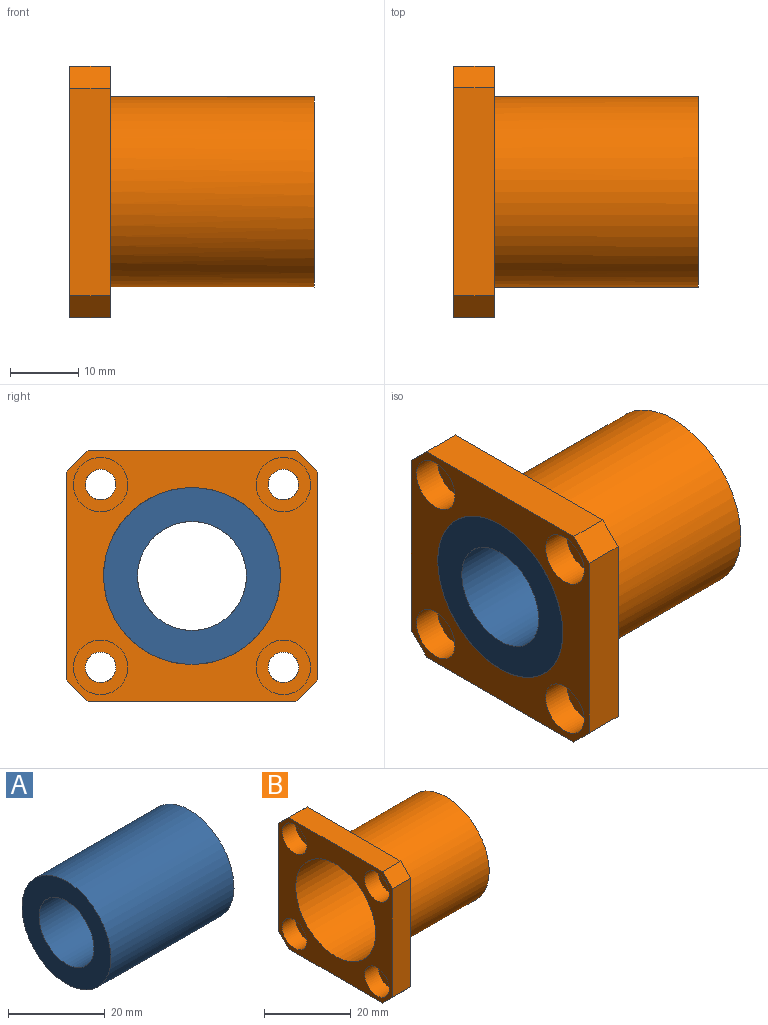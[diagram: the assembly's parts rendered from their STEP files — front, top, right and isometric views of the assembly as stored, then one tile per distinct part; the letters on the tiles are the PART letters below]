
ASSEMBLY  parts=2 mates=1
PART A: 4 faces, bbox 36x26x26 mm
  f0: plane 26x26mm, normal (1,0,0), area 329.9mm2, adj f2,f3
  f1: plane 26x26mm, normal (-1,0,0), area 329.9mm2, adj f2,f3
  f2: cylinder r=13mm len=36mm, axis (-1,0,0), area 2940.5mm2, adj f0,f1
  f3: cylinder r=8mm len=36mm, axis (-1,0,0), area 1809.6mm2, adj f0,f1
PART B: 25 faces, bbox 36x37x37 mm
  f0: cylinder r=2.25mm len=4.5mm, axis (-1,0,0), area 22.6mm2, adj f12,f19
  f1: cylinder r=2.25mm len=4.5mm, axis (-1,0,0), area 22.6mm2, adj f12,f17
  f2: cylinder r=2.25mm len=4.5mm, axis (-1,0,0), area 22.6mm2, adj f12,f15
  f3: cylinder r=2.25mm len=4.5mm, axis (-1,0,0), area 22.6mm2, adj f12,f21
  f4: plane 30.58x6mm, normal (0,0,-1), area 183.5mm2, adj f5,f11,f12,f13
  f5: plane 6x3.21mm, normal (0,0.71,-0.71), area 27.2mm2, adj f4,f6,f12,f13
  f6: plane 30.58x6mm, normal (0,1,0), area 183.5mm2, adj f5,f7,f12,f13
  f7: plane 6x3.21mm, normal (0,0.71,0.71), area 27.2mm2, adj f6,f8,f12,f13
  f8: plane 30.58x6mm, normal (0,0,1), area 183.5mm2, adj f7,f9,f12,f13
  f9: plane 6x3.21mm, normal (0,-0.71,0.71), area 27.2mm2, adj f8,f10,f12,f13
  f10: plane 30.58x6mm, normal (0,-1,0), area 183.5mm2, adj f9,f11,f12,f13
  f11: plane 6x3.21mm, normal (0,-0.71,-0.71), area 27.2mm2, adj f4,f10,f12,f13
  f12: plane 37x37mm, normal (1,0,0), area 669mm2, adj f0,f1,f2,f3,f4,f5,f6,f7
  f13: plane 37x37mm, normal (-1,0,0), area 616.4mm2, adj f4,f5,f6,f7,f8,f9,f10,f11
  f14: cylinder r=4mm len=8mm, axis (-1,0,0), area 110.6mm2, adj f13,f15
  f15: plane 8x8mm, normal (-1,0,0), area 34.4mm2, adj f2,f14
  f16: cylinder r=4mm len=8mm, axis (-1,0,0), area 110.6mm2, adj f13,f17
  f17: plane 8x8mm, normal (-1,0,0), area 34.4mm2, adj f1,f16
  f18: cylinder r=4mm len=8mm, axis (-1,0,0), area 110.6mm2, adj f13,f19
  f19: plane 8x8mm, normal (-1,0,0), area 34.4mm2, adj f0,f18
  f20: cylinder r=4mm len=8mm, axis (-1,0,0), area 110.6mm2, adj f13,f21
  f21: plane 8x8mm, normal (-1,0,0), area 34.4mm2, adj f3,f20
  f22: cylinder r=14mm len=30mm, axis (-1,0,0), area 2638.9mm2, adj f12,f23
  f23: plane 28x28mm, normal (1,0,0), area 84.8mm2, adj f22,f24
  f24: cylinder r=13mm len=36mm, axis (-1,0,0), area 2940.5mm2, adj f13,f23
PLACE A t=(-14.59,-1.18,-4.72)mm
PLACE B t=(-14.59,-1.18,-4.72)mm
MATE fastened A.f3 <-> B.f24  axis (-1,0,0) through (-14.59,-1.18,-4.72)mm
